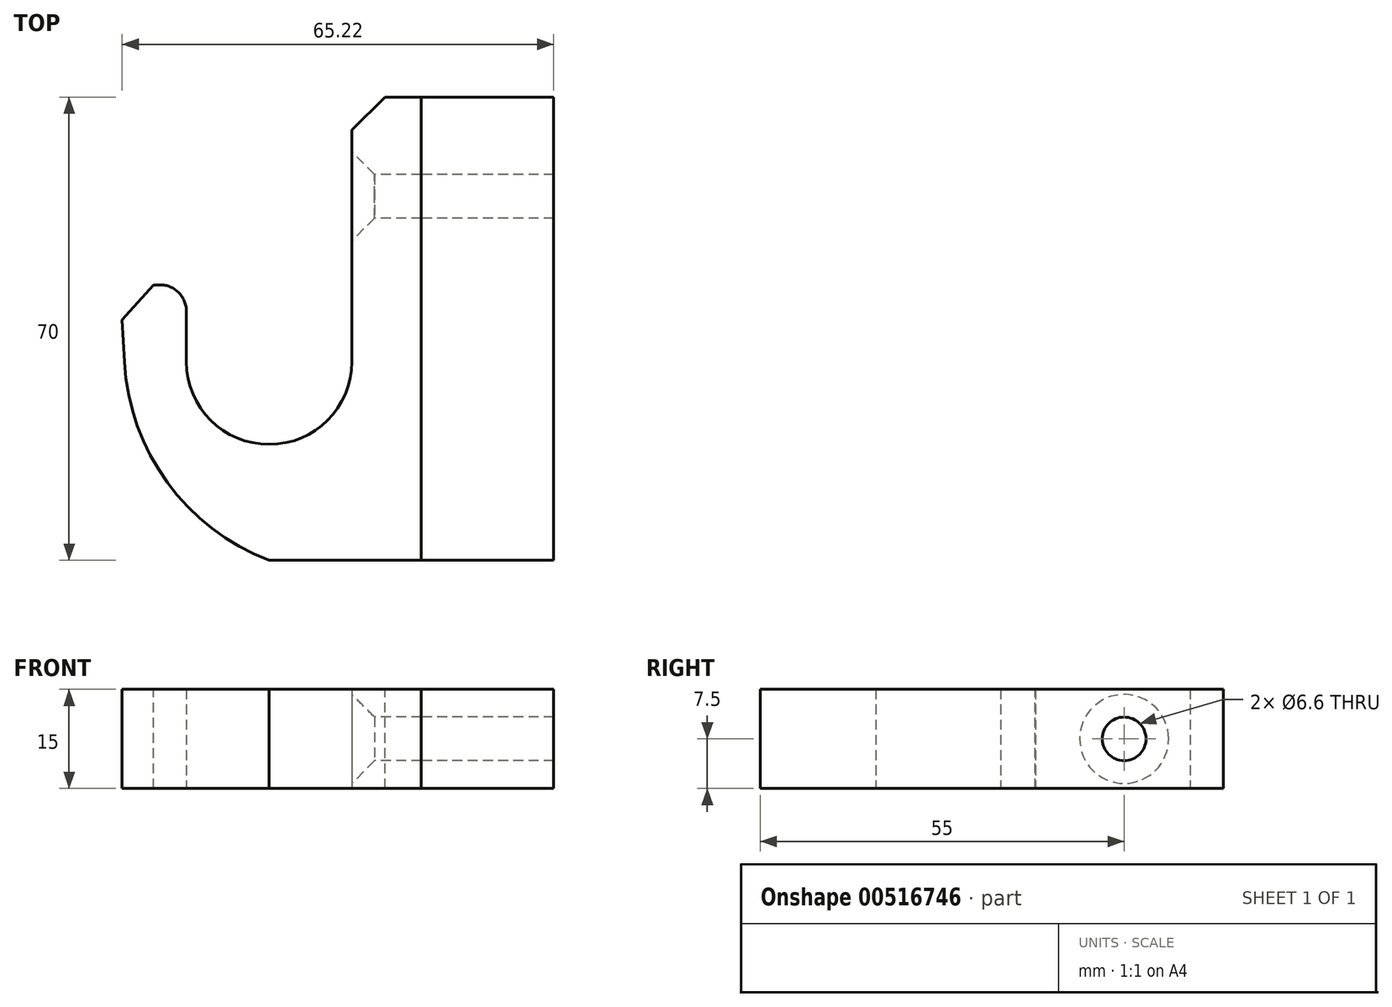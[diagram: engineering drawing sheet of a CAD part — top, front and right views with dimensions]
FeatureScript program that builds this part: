
annotation { "Feature Type Name" : "Feature", "Feature Type Description" : "" }
export const myFeature = defineFeature(function(context is Context, id is Id, definition is map)
    precondition{}
    {
        {
            var Q0;
            Q0=qCreatedBy(makeId("Top.planeOp"),FACE);
            var sketch = newSketch(context, id + "F0", { "sketchPlane" : qUnion([Q0])});
            skLineSegment(sketch, "E0", {"start": v(0, 0) * mm, "end": v(0, 70) * mm});
            skLineSegment(sketch, "E1", {"start": v(0, 70) * mm, "end": v(-10.5, 70) * mm});
            skLineSegment(sketch, "E2", {"start": v(-10.5, 70) * mm, "end": v(-10.5, 30) * mm});
            skArc(sketch, "E3", {"start": v(-35.5, 30) * mm, "mid": v(-23, 17.5) * mm, "end": v(-10.5, 30) * mm});
            skLineSegment(sketch, "E4", {"start": v(-35.5, 30) * mm, "end": v(-35.5, 41.85) * mm});
            skLineSegment(sketch, "E5", {"start": v(-35.5, 41.85) * mm, "end": v(-45.49, 41.31) * mm});
            skLineSegment(sketch, "E6", {"start": v(-45.49, 41.31) * mm, "end": v(-44.88, 30) * mm});
            skLineSegment(sketch, "E7", {"start": v(0, 0) * mm, "end": v(-23, 0) * mm});
            skArc(sketch, "E8", {"start": v(-44.88, 30) * mm, "mid": v(-38.39, 11.76) * mm, "end": v(-23, 0) * mm});
            skSolve(sketch);
        }
        {
            var Q0;
            Q0=makeQuery(id+"F0.imprint","IMPRINT",FACE,{"disambiguationData":[TD([[makeQuery(id+"F0.imprint","IMPRINT",EDGE,{"derivedFrom":sQuery(id+"F0.wireOp",EDGE,"E0")}),1.0]])]});
            extrude(context, id + "F1", {"entities" : qUnion([Q0]), "depth" : 15 * mm, "offsetDistance" : 25 * mm});
        }
        {
            var Q0;
            Q0=makeQuery(id+"F1.opExtrude","SWEPT_FACE",FACE,{"disambiguationData":[OSD([sQuery(id+"F0.wireOp",EDGE,"E2")])]});
            var sketch = newSketch(context, id + "F2", { "sketchPlane" : qUnion([Q0])});
            skPoint(sketch, "E9", {"position": v(-55, 7.5) * mm});
            skLineSegment(sketch, "E10", {"start": v(-71.09, 7.5) * mm, "end": v(-70, 7.5) * mm, "construction": true});
            skSolve(sketch);
        }
        {
            var Q0;
            Q0=sQuery(id+"F2.wireOp",VERTEX,"E9");
            var Q1;
            Q1=makeQuery(id+"F1.opExtrude","SWEPT_BODY",BODY,{"disambiguationData":[OSD([sQuery(id+"F0.wireOp",EDGE,"E0"),sQuery(id+"F0.wireOp",EDGE,"E1"),sQuery(id+"F0.wireOp",EDGE,"E2"),sQuery(id+"F0.wireOp",EDGE,"E3"),sQuery(id+"F0.wireOp",EDGE,"E4"),sQuery(id+"F0.wireOp",EDGE,"E5"),sQuery(id+"F0.wireOp",EDGE,"E6"),sQuery(id+"F0.wireOp",EDGE,"E7"),sQuery(id+"F0.wireOp",EDGE,"E8")])]});
            hole(context, id + "F3", {"style" : HoleStyle.C_SINK, "endStyle" : HoleEndStyle.THROUGH, "standardTappedOrClearance" : lookupTablePath({ "standard" : "ISO", "fit" : "Normal", "size" : "M6", "type" : "Clearance" }), "standardBlindInLast" : lookupTablePath({ "fit" : "Standard", "standard" : "ISO", "size" : "M6", "type" : "Clearance" }), "holeDiameter" : 6.6 * mm, "cSinkDiameter" : 13.44 * mm, "cSinkAngle" : 90 * degree, "majorDiameter" : 5 * mm, "isTappedThrough" : true, "tappedDepth" : 12 * mm, "tapClearance" : 3, "locations" : qUnion([Q0]), "scope" : qUnion([Q1])});
        }
        {
            var Q0;
            Q0=makeQuery(id+"F1.opExtrude","SWEPT_EDGE",EDGE,{"disambiguationData":[OSD([sQuery(id+"F0.wireOp",EDGE,"E1"),sQuery(id+"F0.wireOp",EDGE,"E2")])]});
            chamfer(context, id + "F4", {"entities" : qUnion([Q0]), "width" : 5 * mm, "tangentPropagation" : true});
        }
        {
            var Q0;
            Q0=makeQuery(id+"F1.opExtrude","SWEPT_EDGE",EDGE,{"disambiguationData":[OSD([sQuery(id+"F0.wireOp",EDGE,"E5"),sQuery(id+"F0.wireOp",EDGE,"E6")])]});
            chamfer(context, id + "F5", {"entities" : qUnion([Q0]), "width" : 5 * mm, "tangentPropagation" : true});
        }
        {
            var Q0;
            Q0=makeQuery(id+"F1.opExtrude","SWEPT_EDGE",EDGE,{"disambiguationData":[OSD([sQuery(id+"F0.wireOp",EDGE,"E4"),sQuery(id+"F0.wireOp",EDGE,"E5")])]});
            fillet(context, id + "F6", {"entities" : qUnion([Q0]), "radius" : 4 * mm, "tangentPropagation" : true, "allowEdgeOverflow" : false});
        }
        {
            var Q0;
            Q0=makeQuery(id+"F1.opExtrude","SWEPT_FACE",FACE,{"disambiguationData":[OSD([sQuery(id+"F0.wireOp",EDGE,"E0")])]});
            var sketch = newSketch(context, id + "F7", { "sketchPlane" : qUnion([Q0])});
            skLineSegment(sketch, "E11.0.0", {"start": v(0, 0) * mm, "end": v(70, 0) * mm});
            skLineSegment(sketch, "E11.0.1", {"start": v(70, 0) * mm, "end": v(70, 15) * mm});
            skLineSegment(sketch, "E11.0.2", {"start": v(70, 15) * mm, "end": v(0, 15) * mm});
            skLineSegment(sketch, "E11.0.3", {"start": v(0, 15) * mm, "end": v(0, 0) * mm});
            skCircle(sketch, "E12.0", {"center": v(55, 7.5) * mm, "radius": 3.3 * mm});
            skSolve(sketch);
        }
        {
            var Q0;
            Q0=makeQuery(id+"F7.imprint","IMPRINT",FACE,{"disambiguationData":[TD([[makeQuery(id+"F7.imprint","IMPRINT",EDGE,{"derivedFrom":sQuery(id+"F7.wireOp",EDGE,"E11.0.0")}),1.0]])]});
            extrude(context, id + "F8", {"entities" : qUnion([Q0]), "depth" : 20 * mm, "offsetDistance" : 25 * mm});
        }
    });
